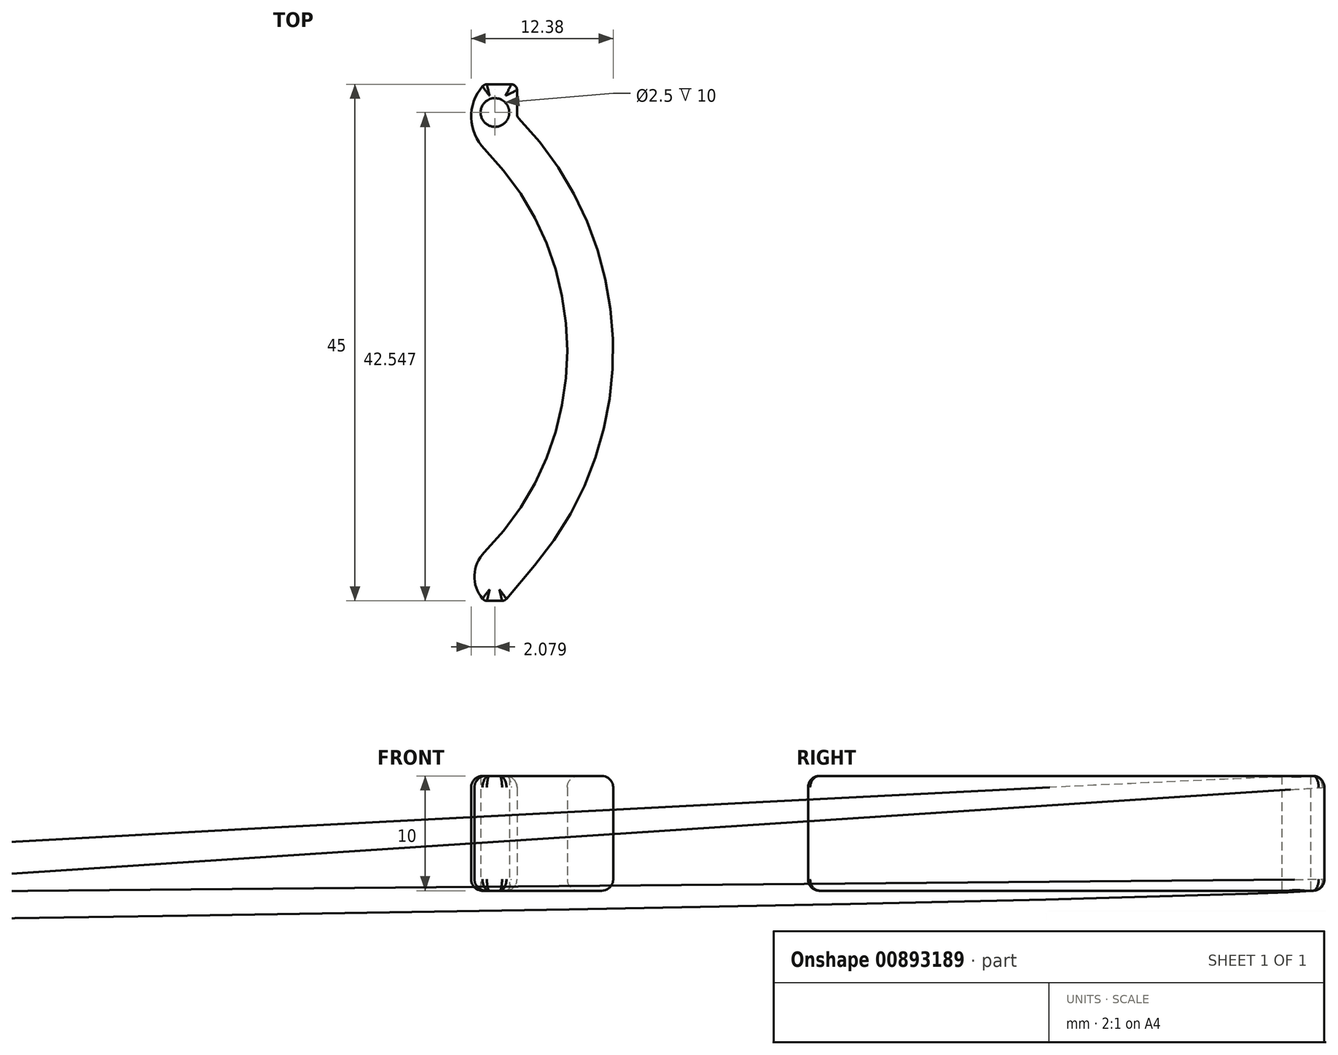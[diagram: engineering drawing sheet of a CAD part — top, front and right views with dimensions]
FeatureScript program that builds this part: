
annotation { "Feature Type Name" : "Feature", "Feature Type Description" : "" }
export const myFeature = defineFeature(function(context is Context, id is Id, definition is map)
    precondition{}
    {
        {
            var Q0;
            Q0=qCreatedBy(makeId("Top.planeOp"),FACE);
            var sketch = newSketch(context, id + "F0", { "sketchPlane" : qUnion([Q0])});
            skArc(sketch, "E0", {"start": v(0, -44.59) * mm, "mid": v(7.22, -27.01) * mm, "end": v(0, -9.43) * mm});
            skArc(sketch, "E1", {"start": v(-0.16, -3.98) * mm, "mid": v(-1.15, -6.74) * mm, "end": v(0, -9.43) * mm});
            skArc(sketch, "E2", {"start": v(0, -44.59) * mm, "mid": v(-0.86, -46.58) * mm, "end": v(-0.16, -48.63) * mm});
            skArc(sketch, "E3.0", {"start": v(4.37, -45.73) * mm, "mid": v(11.2, -25.98) * mm, "end": v(2.99, -6.76) * mm});
            skLineSegment(sketch, "E4", {"start": v(0.22, -48.8) * mm, "end": v(1.54, -48.8) * mm});
            skLineSegment(sketch, "E5", {"start": v(1.92, -48.63) * mm, "end": v(4.37, -45.73) * mm});
            skPoint(sketch, "E6.visualSharp", {"position": v(1.77, -48.8) * mm});
            skArc(sketch, "E6.filletArc", {"start": v(1.54, -48.8) * mm, "mid": v(1.75, -48.76) * mm, "end": v(1.92, -48.63) * mm});
            skPoint(sketch, "E7.visualSharp", {"position": v(0, -48.8) * mm});
            skArc(sketch, "E7.filletArc", {"start": v(-0.16, -48.63) * mm, "mid": v(0, -48.76) * mm, "end": v(0.22, -48.8) * mm});
            skLineSegment(sketch, "E8", {"start": v(0.22, -3.8) * mm, "end": v(2.34, -3.8) * mm});
            skLineSegment(sketch, "E9", {"start": v(2.84, -4.3) * mm, "end": v(2.84, -6.42) * mm});
            skArc(sketch, "E10.filletArc", {"start": v(2.84, -6.42) * mm, "mid": v(2.88, -6.6) * mm, "end": v(2.99, -6.76) * mm});
            skPoint(sketch, "E11.visualSharp", {"position": v(2.84, -3.8) * mm});
            skArc(sketch, "E11.filletArc", {"start": v(2.84, -4.3) * mm, "mid": v(2.7, -3.95) * mm, "end": v(2.34, -3.8) * mm});
            skPoint(sketch, "E12.visualSharp", {"position": v(0, -3.8) * mm});
            skArc(sketch, "E12.filletArc", {"start": v(0.22, -3.8) * mm, "mid": v(0.01, -3.85) * mm, "end": v(-0.16, -3.98) * mm});
            skCircle(sketch, "E13", {"center": v(0.92, -6.26) * mm, "radius": 1.25 * mm});
            skSolve(sketch);
        }
        {
            var Q0;
            Q0 = qSketchRegion(id + "F0", true);
            var Q1;
            Q1 = qConstructionFilter(qBodyType(qCreatedBy(id + "F0" ,EDGE), BodyType.WIRE), ConstructionObject.NO);
            extrude(context, id + "F1", {"entities" : qUnion([Q0]), "surfaceEntities" : qUnion([Q1]), "depth" : 10 * mm, "offsetDistance" : 25 * mm});
        }
        {
            var Q0;
            Q0=makeQuery(id+"F1.opExtrude","SWEPT_FACE",FACE,{"disambiguationData":[OSD([sQuery(id+"F0.wireOp",EDGE,"E0")])]});
            fillet(context, id + "F2", {"entities" : qUnion([Q0]), "radius" : 1 * mm, "tangentPropagation" : true, "allowEdgeOverflow" : false});
        }
    });
